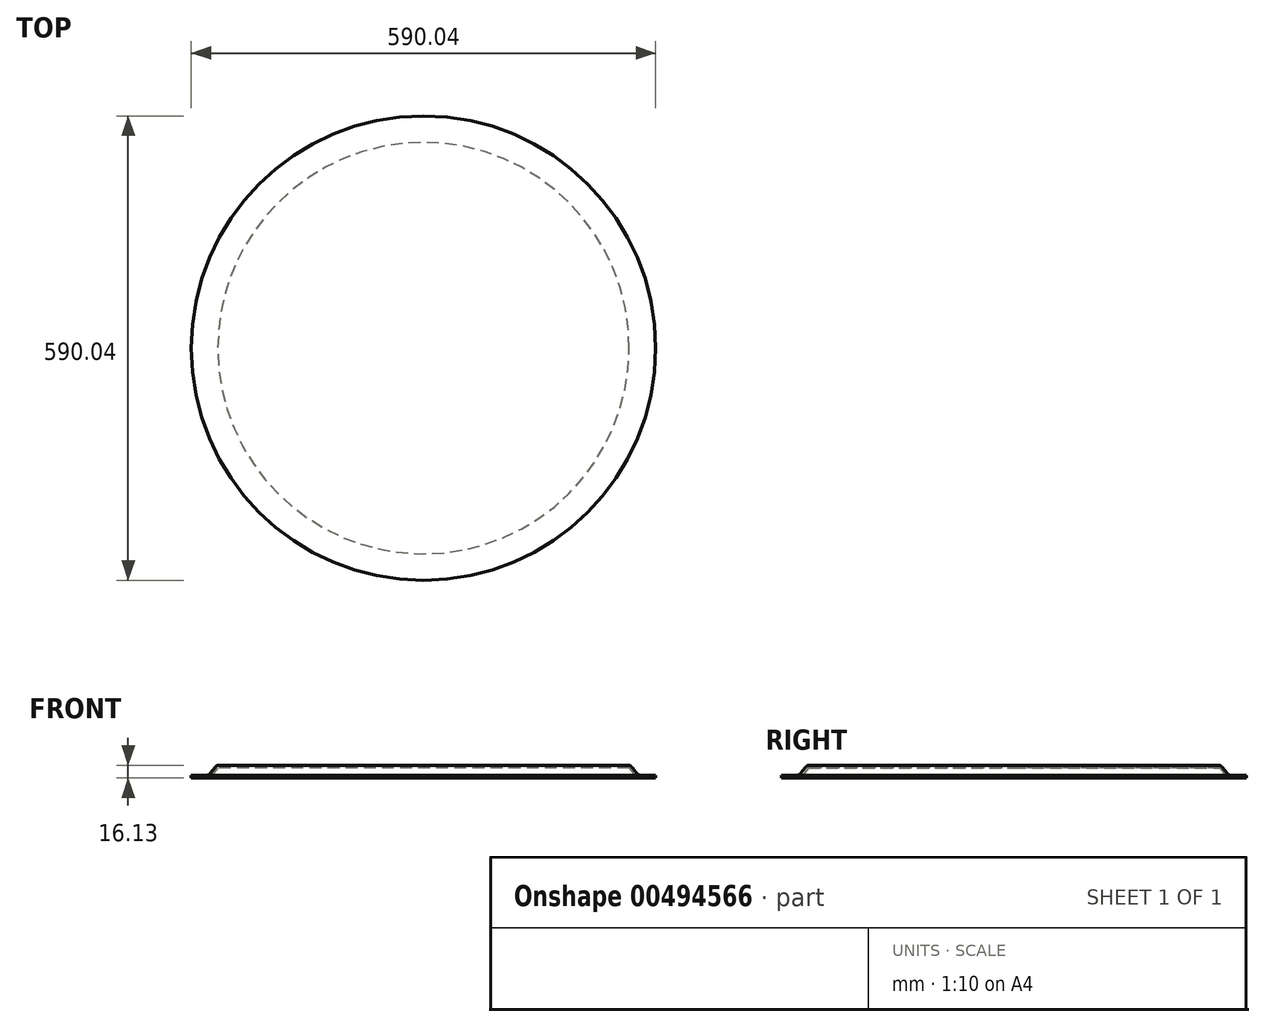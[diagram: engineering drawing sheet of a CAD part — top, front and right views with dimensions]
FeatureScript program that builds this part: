
annotation { "Feature Type Name" : "Feature", "Feature Type Description" : "" }
export const myFeature = defineFeature(function(context is Context, id is Id, definition is map)
    precondition{}
    {
        {
            var Q0;
            Q0=qCreatedBy(makeId("Front.planeOp"),FACE);
            var sketch = newSketch(context, id + "F0", { "sketchPlane" : qUnion([Q0])});
            skLineSegment(sketch, "E0", {"start": v(0, 0) * mm, "end": v(259.86, 0) * mm});
            skLineSegment(sketch, "E1", {"start": v(275.97, -12.7) * mm, "end": v(295.02, -12.7) * mm});
            skLineSegment(sketch, "E2", {"start": v(264.86, -2.44) * mm, "end": v(270.97, -10.26) * mm});
            skPoint(sketch, "E3.visualSharp", {"position": v(262.96, 0) * mm});
            skArc(sketch, "E3.filletArc", {"start": v(264.86, -2.44) * mm, "mid": v(262.64, -0.64) * mm, "end": v(259.86, 0) * mm});
            skPoint(sketch, "E4.visualSharp", {"position": v(272.87, -12.7) * mm});
            skArc(sketch, "E4.filletArc", {"start": v(270.97, -10.26) * mm, "mid": v(273.19, -12.06) * mm, "end": v(275.97, -12.7) * mm});
            skLineSegment(sketch, "E5.0", {"start": v(275.97, -16.13) * mm, "end": v(295.02, -16.13) * mm});
            skArc(sketch, "E5.1", {"start": v(268.26, -12.37) * mm, "mid": v(271.68, -15.14) * mm, "end": v(275.97, -16.13) * mm});
            skLineSegment(sketch, "E5.2", {"start": v(261.28, -3.43) * mm, "end": v(268.26, -12.37) * mm});
            skLineSegment(sketch, "E5.3", {"start": v(0, -3.43) * mm, "end": v(261.28, -3.43) * mm});
            skLineSegment(sketch, "E6", {"start": v(0, 0) * mm, "end": v(0, -3.43) * mm});
            skLineSegment(sketch, "E7", {"start": v(295.02, -12.7) * mm, "end": v(295.02, -16.13) * mm});
            skSolve(sketch);
        }
        {
            var Q0;
            Q0 = qSketchRegion(id + "F0", true);
            var Q1;
            Q1=sQuery(id+"F0.wireOp",EDGE,"E6");
            revolve(context, id + "F1", {"entities" : qUnion([Q0]), "axis" : qUnion([Q1]), "revolveType" : RevolveType.FULL});
        }
    });
